# Revit family: SSF type 1,2,3,5 and 6
name_source: partatom
category: Windows
revit_build: Autodesk Revit LT 2016 (Build: 20150220_1215(x64)
units: mm (PartAtom-declared; Revit-internal decimal feet)

## family parameters
Always vertical = Yes
Cut with Voids When Loaded = No
Host = Wall
OmniClass Number = 23.30.20.00
OmniClass Title = Windows
Room Calculation Point = No
Shared = No

## types (30) — shared parameters
Default Sill Height = 914.4 mm  [stored 3 ft]
Frame putty = Glazing putty
GB 2 = 922.2 mm
GB 3 = 1390.2 mm
GB 4 = 1856.2 mm
Glass = Glass
Glazing 3 = Yes
Glazing bar = Steel dipped in Grey oxide
Glazing bar 6 = No
Manufacturer = Robmeg
Vert GB LT = No
Vert GB RT = No
Wall Closure = By host

## per-type parameters (varying)
- SS type- SSF56: Description=Industrial steel window; GB 1=456.2 mm; GB 5=2322.2 mm; GB 6=2790.2 mm; GB LT=780.6 mm; GB RT=780.6 mm; Glazing 1=Yes; Glazing 10=Yes; Glazing 11=Yes; Glazing 12=Yes; Glazing 13=Yes; Glazing 14=Yes; Glazing 15=Yes; Glazing 16=Yes; Glazing 17=Yes; Glazing 18=Yes; Glazing 19=Yes; Glazing 2=Yes; Glazing 20=Yes; Glazing 21=Yes; Glazing 22=Yes; Glazing 23=Yes; Glazing 24=Yes; Glazing 25=Yes; Glazing 26=Yes; Glazing 27=Yes; Glazing 28=Yes; Glazing 29=Yes; Glazing 30=Yes; Glazing 4=Yes; Glazing 5=Yes; Glazing 6=Yes; Glazing 7=Yes; Glazing 8=Yes; Glazing 9=Yes; Glazing bar 1=Yes; Glazing bar 2=Yes; Glazing bar 3=Yes; Glazing bar 4=Yes; Glazing bar 5=Yes; Height=2842 mm  [stored 9.32415 ft]; Model=SSF56; URL=www.robmeg.co.za; Vert GB 1=Yes; Vert GB 2=Yes; Vert GB 3=Yes; Vert GB 4=Yes; Vert bar 1=468.36 mm; Vert bar 2=156.12 mm; Vert bar 3=156.12 mm; Vert bar 4=468.36 mm; Width=1613 mm  [stored 5.29199 ft]
- SS type- SSF55: Description=Industrial steel window; GB 1=456.2 mm; GB 5=2322.2 mm; GB 6=2527.2 mm; GB LT=780.6 mm; GB RT=780.6 mm; Glazing 1=Yes; Glazing 10=Yes; Glazing 11=Yes; Glazing 12=Yes; Glazing 13=Yes; Glazing 14=Yes; Glazing 15=Yes; Glazing 16=Yes; Glazing 17=Yes; Glazing 18=Yes; Glazing 19=Yes; Glazing 2=Yes; Glazing 20=Yes; Glazing 21=Yes; Glazing 22=Yes; Glazing 23=Yes; Glazing 24=Yes; Glazing 25=Yes; Glazing 26=No; Glazing 27=No; Glazing 28=No; Glazing 29=No; Glazing 30=No; Glazing 4=Yes; Glazing 5=Yes; Glazing 6=Yes; Glazing 7=Yes; Glazing 8=Yes; Glazing 9=Yes; Glazing bar 1=Yes; Glazing bar 2=Yes; Glazing bar 3=Yes; Glazing bar 4=Yes; Glazing bar 5=No; Height=2374 mm  [stored 7.78871 ft]; Model=SSF55; URL=www.robmeg.co.za; Vert GB 1=Yes; Vert GB 2=Yes; Vert GB 3=Yes; Vert GB 4=Yes; Vert bar 1=468.36 mm; Vert bar 2=156.12 mm; Vert bar 3=156.12 mm; Vert bar 4=468.36 mm; Width=1613 mm  [stored 5.29199 ft]
- SS type- SSF54: Description=Industrial steel window; GB 1=547.2 mm; GB 5=2322.2 mm; GB 6=2527.2 mm; GB LT=780.6 mm; GB RT=780.6 mm; Glazing 1=Yes; Glazing 10=Yes; Glazing 11=Yes; Glazing 12=Yes; Glazing 13=Yes; Glazing 14=Yes; Glazing 15=Yes; Glazing 16=Yes; Glazing 17=Yes; Glazing 18=Yes; Glazing 19=Yes; Glazing 2=Yes; Glazing 20=Yes; Glazing 21=No; Glazing 22=No; Glazing 23=No; Glazing 24=No; Glazing 25=No; Glazing 26=No; Glazing 27=No; Glazing 28=No; Glazing 29=No; Glazing 30=No; Glazing 4=Yes; Glazing 5=Yes; Glazing 6=Yes; Glazing 7=Yes; Glazing 8=Yes; Glazing 9=Yes; Glazing bar 1=Yes; Glazing bar 2=Yes; Glazing bar 3=Yes; Glazing bar 4=No; Glazing bar 5=No; Height=1908 mm  [stored 6.25984 ft]; Model=SSF54; URL=www.robmeg.co.za; Vert GB 1=Yes; Vert GB 2=Yes; Vert GB 3=Yes; Vert GB 4=Yes; Vert bar 1=468.36 mm; Vert bar 2=156.12 mm; Vert bar 3=156.12 mm; Vert bar 4=468.36 mm; Width=1613 mm  [stored 5.29199 ft]
- SS type- SSF53: Description=Industrial steel window; GB 1=547.2 mm; GB 5=2322.2 mm; GB 6=2527.2 mm; GB LT=780.6 mm; GB RT=780.6 mm; Glazing 1=Yes; Glazing 10=Yes; Glazing 11=Yes; Glazing 12=Yes; Glazing 13=Yes; Glazing 14=Yes; Glazing 15=Yes; Glazing 16=No; Glazing 17=No; Glazing 18=No; Glazing 19=No; Glazing 2=Yes; Glazing 20=No; Glazing 21=No; Glazing 22=No; Glazing 23=No; Glazing 24=No; Glazing 25=No; Glazing 26=No; Glazing 27=No; Glazing 28=No; Glazing 29=No; Glazing 30=No; Glazing 4=Yes; Glazing 5=Yes; Glazing 6=Yes; Glazing 7=Yes; Glazing 8=Yes; Glazing 9=Yes; Glazing bar 1=Yes; Glazing bar 2=Yes; Glazing bar 3=No; Glazing bar 4=No; Glazing bar 5=No; Height=1442 mm  [stored 4.73097 ft]; Model=SSF53; URL=www.robmeg.co.za; Vert GB 1=Yes; Vert GB 2=Yes; Vert GB 3=Yes; Vert GB 4=Yes; Vert bar 1=468.36 mm; Vert bar 2=156.12 mm; Vert bar 3=156.12 mm; Vert bar 4=468.36 mm; Width=1613 mm  [stored 5.29199 ft]
- SS type- SSF52: Description=Industrial steel window; GB 1=547.2 mm; GB 5=2322.2 mm; GB 6=2527.2 mm; GB LT=780.6 mm; GB RT=780.6 mm; Glazing 1=Yes; Glazing 10=Yes; Glazing 11=No; Glazing 12=No; Glazing 13=No; Glazing 14=No; Glazing 15=No; Glazing 16=No; Glazing 17=No; Glazing 18=No; Glazing 19=No; Glazing 2=Yes; Glazing 20=No; Glazing 21=No; Glazing 22=No; Glazing 23=No; Glazing 24=No; Glazing 25=No; Glazing 26=No; Glazing 27=No; Glazing 28=No; Glazing 29=No; Glazing 30=No; Glazing 4=Yes; Glazing 5=Yes; Glazing 6=Yes; Glazing 7=Yes; Glazing 8=Yes; Glazing 9=Yes; Glazing bar 1=Yes; Glazing bar 2=No; Glazing bar 3=No; Glazing bar 4=No; Glazing bar 5=No; Height=974 mm  [stored 3.19554 ft]; Model=SSF52; URL=www.robmeg.co.za; Vert GB 1=Yes; Vert GB 2=Yes; Vert GB 3=Yes; Vert GB 4=Yes; Vert bar 1=468.36 mm; Vert bar 2=156.12 mm; Vert bar 3=156.12 mm; Vert bar 4=468.36 mm; Width=1613 mm  [stored 5.29199 ft]
- SS type- SSF51: Description=Industrial steel window; GB 1=456.2 mm; GB 5=2322.2 mm; GB 6=2527.2 mm; GB LT=780.6 mm; GB RT=780.6 mm; Glazing 1=Yes; Glazing 10=No; Glazing 11=No; Glazing 12=No; Glazing 13=No; Glazing 14=No; Glazing 15=No; Glazing 16=No; Glazing 17=No; Glazing 18=No; Glazing 19=No; Glazing 2=Yes; Glazing 20=No; Glazing 21=No; Glazing 22=No; Glazing 23=No; Glazing 24=No; Glazing 25=No; Glazing 26=No; Glazing 27=No; Glazing 28=No; Glazing 29=No; Glazing 30=No; Glazing 4=Yes; Glazing 5=Yes; Glazing 6=No; Glazing 7=No; Glazing 8=No; Glazing 9=No; Glazing bar 1=No; Glazing bar 2=No; Glazing bar 3=No; Glazing bar 4=No; Glazing bar 5=No; Height=508 mm; Model=SSF51; URL=www.robmeg.co.za; Vert GB 1=Yes; Vert GB 2=Yes; Vert GB 3=Yes; Vert GB 4=Yes; Vert bar 1=468.36 mm; Vert bar 2=156.12 mm; Vert bar 3=156.12 mm; Vert bar 4=468.36 mm; Width=1613 mm  [stored 5.29199 ft]
- SS type- SSF46: Description=Industrial steel window; GB 1=456.2 mm; GB 5=2322.2 mm; GB 6=2790.2 mm; GB LT=780.6 mm; GB RT=623.6 mm; Glazing 1=No; Glazing 10=Yes; Glazing 11=No; Glazing 12=Yes; Glazing 13=Yes; Glazing 14=Yes; Glazing 15=Yes; Glazing 16=No; Glazing 17=Yes; Glazing 18=Yes; Glazing 19=Yes; Glazing 2=Yes; Glazing 20=Yes; Glazing 21=No; Glazing 22=Yes; Glazing 23=Yes; Glazing 24=Yes; Glazing 25=Yes; Glazing 26=No; Glazing 27=Yes; Glazing 28=Yes; Glazing 29=Yes; Glazing 30=Yes; Glazing 4=Yes; Glazing 5=Yes; Glazing 6=No; Glazing 7=Yes; Glazing 8=Yes; Glazing 9=Yes; Glazing bar 1=Yes; Glazing bar 2=Yes; Glazing bar 3=Yes; Glazing bar 4=Yes; Glazing bar 5=Yes; Height=2842 mm  [stored 9.32415 ft]; Model=SSF46; URL=www.robmeg.co.za; Vert GB 1=Yes; Vert GB 2=Yes; Vert GB 3=Yes; Vert GB 4=No; Vert bar 1=311.8 mm  [stored 1.02297 ft]; Vert bar 2=0 mm  [stored 0 ft]; Vert bar 3=311.8 mm  [stored 1.02297 ft]; Vert bar 4=623.6 mm; Width=1299 mm  [stored 4.26181 ft]
- SS type- SSF36: Description=Indsutrial steel window; GB 1=456.2 mm; GB 5=2322.2 mm; GB 6=2789.2 mm; GB LT=580.6 mm; GB RT=699.6 mm; Glazing 1=No; Glazing 10=No; Glazing 11=No; Glazing 12=Yes; Glazing 13=Yes; Glazing 14=Yes; Glazing 15=No; Glazing 16=No; Glazing 17=Yes; Glazing 18=Yes; Glazing 19=Yes; Glazing 2=Yes; Glazing 20=No; Glazing 21=No; Glazing 22=Yes; Glazing 23=Yes; Glazing 24=Yes; Glazing 25=No; Glazing 26=No; Glazing 27=Yes; Glazing 28=Yes; Glazing 29=Yes; Glazing 30=No; Glazing 4=Yes; Glazing 5=No; Glazing 6=No; Glazing 7=Yes; Glazing 8=Yes; Glazing 9=Yes; Glazing bar 1=Yes; Glazing bar 2=Yes; Glazing bar 3=Yes; Glazing bar 4=Yes; Glazing bar 5=Yes; Height=2842 mm  [stored 9.32415 ft]; Model=SSF36; URL=www.robmeg.co.za; Vert GB 1=No; Vert GB 2=Yes; Vert GB 3=Yes; Vert GB 4=No; Vert bar 1=468.36 mm; Vert bar 2=156.12 mm; Vert bar 3=156.12 mm; Vert bar 4=468.36 mm; Width=984 mm  [stored 3.22835 ft]
- SS type- SSF45: Description=Industrial steel window; GB 1=456.2 mm; GB 5=2323.2 mm; GB 6=2790.2 mm; GB LT=780.6 mm; GB RT=623.6 mm; Glazing 1=No; Glazing 10=Yes; Glazing 11=No; Glazing 12=Yes; Glazing 13=Yes; Glazing 14=Yes; Glazing 15=Yes; Glazing 16=No; Glazing 17=Yes; Glazing 18=Yes; Glazing 19=Yes; Glazing 2=Yes; Glazing 20=Yes; Glazing 21=No; Glazing 22=Yes; Glazing 23=Yes; Glazing 24=Yes; Glazing 25=Yes; Glazing 26=No; Glazing 27=No; Glazing 28=No; Glazing 29=No; Glazing 30=No; Glazing 4=Yes; Glazing 5=Yes; Glazing 6=No; Glazing 7=Yes; Glazing 8=Yes; Glazing 9=Yes; Glazing bar 1=Yes; Glazing bar 2=Yes; Glazing bar 3=Yes; Glazing bar 4=Yes; Glazing bar 5=No; Height=2375 mm; Model=SSF45; URL=www.robmeg.co.za; Vert GB 1=Yes; Vert GB 2=Yes; Vert GB 3=Yes; Vert GB 4=No; Vert bar 1=311.8 mm  [stored 1.02297 ft]; Vert bar 2=0 mm  [stored 0 ft]; Vert bar 3=311.8 mm  [stored 1.02297 ft]; Vert bar 4=623.6 mm; Width=1299 mm  [stored 4.26181 ft]
- SS type- SSF44: GB 1=456.2 mm; GB 5=2323.2 mm; GB 6=2790.2 mm; GB LT=780.6 mm; GB RT=623.6 mm; Glazing 1=No; Glazing 10=Yes; Glazing 11=No; Glazing 12=Yes; Glazing 13=Yes; Glazing 14=Yes; Glazing 15=Yes; Glazing 16=No; Glazing 17=Yes; Glazing 18=Yes; Glazing 19=Yes; Glazing 2=Yes; Glazing 20=Yes; Glazing 21=No; Glazing 22=No; Glazing 23=No; Glazing 24=No; Glazing 25=No; Glazing 26=No; Glazing 27=No; Glazing 28=No; Glazing 29=No; Glazing 30=No; Glazing 4=Yes; Glazing 5=Yes; Glazing 6=No; Glazing 7=Yes; Glazing 8=Yes; Glazing 9=Yes; Glazing bar 1=Yes; Glazing bar 2=Yes; Glazing bar 3=Yes; Glazing bar 4=No; Glazing bar 5=No; Height=1908 mm  [stored 6.25984 ft]; Vert GB 1=Yes; Vert GB 2=Yes; Vert GB 3=Yes; Vert GB 4=No; Vert bar 1=311.8 mm  [stored 1.02297 ft]; Vert bar 2=0 mm  [stored 0 ft]; Vert bar 3=311.8 mm  [stored 1.02297 ft]; Vert bar 4=623.6 mm; Width=1299 mm  [stored 4.26181 ft]
- SS type- SSF43: Description=Industrial steel window; GB 1=456.2 mm; GB 5=2323.2 mm; GB 6=2790.2 mm; GB LT=780.6 mm; GB RT=623.6 mm; Glazing 1=No; Glazing 10=Yes; Glazing 11=No; Glazing 12=Yes; Glazing 13=Yes; Glazing 14=Yes; Glazing 15=Yes; Glazing 16=No; Glazing 17=No; Glazing 18=Yes; Glazing 19=No; Glazing 2=Yes; Glazing 20=No; Glazing 21=No; Glazing 22=No; Glazing 23=No; Glazing 24=No; Glazing 25=No; Glazing 26=No; Glazing 27=No; Glazing 28=No; Glazing 29=No; Glazing 30=No; Glazing 4=Yes; Glazing 5=Yes; Glazing 6=No; Glazing 7=Yes; Glazing 8=Yes; Glazing 9=Yes; Glazing bar 1=Yes; Glazing bar 2=Yes; Glazing bar 3=No; Glazing bar 4=No; Glazing bar 5=No; Height=1442 mm  [stored 4.73097 ft]; Model=SSF43; URL=www.robmeg.co.za; Vert GB 1=Yes; Vert GB 2=Yes; Vert GB 3=Yes; Vert GB 4=No; Vert bar 1=311.8 mm  [stored 1.02297 ft]; Vert bar 2=0 mm  [stored 0 ft]; Vert bar 3=311.8 mm  [stored 1.02297 ft]; Vert bar 4=623.6 mm; Width=1299 mm  [stored 4.26181 ft]
- SS type- SSF42: Description=Industrial steel window; GB 1=456.2 mm; GB 5=2323.2 mm; GB 6=2790.2 mm; GB LT=780.6 mm; GB RT=623.6 mm; Glazing 1=No; Glazing 10=Yes; Glazing 11=No; Glazing 12=No; Glazing 13=Yes; Glazing 14=No; Glazing 15=No; Glazing 16=No; Glazing 17=No; Glazing 18=No; Glazing 19=No; Glazing 2=Yes; Glazing 20=No; Glazing 21=No; Glazing 22=No; Glazing 23=No; Glazing 24=No; Glazing 25=No; Glazing 26=No; Glazing 27=No; Glazing 28=No; Glazing 29=No; Glazing 30=No; Glazing 4=Yes; Glazing 5=Yes; Glazing 6=No; Glazing 7=Yes; Glazing 8=Yes; Glazing 9=Yes; Glazing bar 1=Yes; Glazing bar 2=No; Glazing bar 3=No; Glazing bar 4=No; Glazing bar 5=No; Height=975 mm  [stored 3.19882 ft]; Model=SSF42; URL=www.robmeg.co.za; Vert GB 1=Yes; Vert GB 2=Yes; Vert GB 3=Yes; Vert GB 4=No; Vert bar 1=311.8 mm  [stored 1.02297 ft]; Vert bar 2=0 mm  [stored 0 ft]; Vert bar 3=311.8 mm  [stored 1.02297 ft]; Vert bar 4=623.6 mm; Width=1299 mm  [stored 4.26181 ft]
- SS type- SSF41: Description=Industrial steel window; GB 1=456.2 mm; GB 5=2323.2 mm; GB 6=2790.2 mm; GB LT=780.6 mm; GB RT=623.6 mm; Glazing 1=No; Glazing 10=No; Glazing 11=No; Glazing 12=No; Glazing 13=No; Glazing 14=No; Glazing 15=No; Glazing 16=No; Glazing 17=No; Glazing 18=No; Glazing 19=No; Glazing 2=Yes; Glazing 20=No; Glazing 21=No; Glazing 22=No; Glazing 23=No; Glazing 24=No; Glazing 25=No; Glazing 26=No; Glazing 27=No; Glazing 28=No; Glazing 29=No; Glazing 30=No; Glazing 4=Yes; Glazing 5=Yes; Glazing 6=No; Glazing 7=No; Glazing 8=No; Glazing 9=No; Glazing bar 1=No; Glazing bar 2=No; Glazing bar 3=No; Glazing bar 4=No; Glazing bar 5=No; Height=508 mm; Model=SSF41; URL=www.robmeg.co.za; Vert GB 1=Yes; Vert GB 2=Yes; Vert GB 3=Yes; Vert GB 4=No; Vert bar 1=311.8 mm  [stored 1.02297 ft]; Vert bar 2=0 mm  [stored 0 ft]; Vert bar 3=311.8 mm  [stored 1.02297 ft]; Vert bar 4=623.6 mm; Width=1299 mm  [stored 4.26181 ft]
- SS type- SSF35: Description=Industrial steel windows; GB 1=456.2 mm; GB 5=2322.2 mm; GB 6=2789.2 mm; GB LT=580.6 mm; GB RT=699.6 mm; Glazing 1=No; Glazing 10=No; Glazing 11=No; Glazing 12=Yes; Glazing 13=Yes; Glazing 14=Yes; Glazing 15=No; Glazing 16=No; Glazing 17=Yes; Glazing 18=Yes; Glazing 19=Yes; Glazing 2=Yes; Glazing 20=No; Glazing 21=No; Glazing 22=Yes; Glazing 23=Yes; Glazing 24=Yes; Glazing 25=No; Glazing 26=No; Glazing 27=No; Glazing 28=No; Glazing 29=No; Glazing 30=No; Glazing 4=Yes; Glazing 5=No; Glazing 6=No; Glazing 7=Yes; Glazing 8=Yes; Glazing 9=Yes; Glazing bar 1=Yes; Glazing bar 2=Yes; Glazing bar 3=Yes; Glazing bar 4=Yes; Glazing bar 5=No; Height=2375 mm; Model=SSF35; URL=www.robmeg.co.za; Vert GB 1=No; Vert GB 2=Yes; Vert GB 3=Yes; Vert GB 4=No; Vert bar 1=468.36 mm; Vert bar 2=156.12 mm; Vert bar 3=156.12 mm; Vert bar 4=468.36 mm; Width=984 mm  [stored 3.22835 ft]
- SS type- SSF34: Description=Industrial steel windows; GB 1=456.2 mm; GB 5=2322.2 mm; GB 6=2789.2 mm; GB LT=580.6 mm; GB RT=699.6 mm; Glazing 1=No; Glazing 10=No; Glazing 11=No; Glazing 12=Yes; Glazing 13=Yes; Glazing 14=Yes; Glazing 15=No; Glazing 16=No; Glazing 17=Yes; Glazing 18=Yes; Glazing 19=Yes; Glazing 2=Yes; Glazing 20=No; Glazing 21=No; Glazing 22=No; Glazing 23=No; Glazing 24=No; Glazing 25=No; Glazing 26=No; Glazing 27=No; Glazing 28=No; Glazing 29=No; Glazing 30=No; Glazing 4=Yes; Glazing 5=No; Glazing 6=No; Glazing 7=Yes; Glazing 8=Yes; Glazing 9=Yes; Glazing bar 1=Yes; Glazing bar 2=Yes; Glazing bar 3=Yes; Glazing bar 4=No; Glazing bar 5=No; Height=1908 mm  [stored 6.25984 ft]; Model=SSF34; URL=www.robmeg.co.za; Vert GB 1=No; Vert GB 2=Yes; Vert GB 3=Yes; Vert GB 4=No; Vert bar 1=468.36 mm; Vert bar 2=156.12 mm; Vert bar 3=156.12 mm; Vert bar 4=468.36 mm; Width=984 mm  [stored 3.22835 ft]
- SS type- SSF33: Description=Industrial steel windows; GB 1=456.2 mm; GB 5=2322.2 mm; GB 6=2789.2 mm; GB LT=580.6 mm; GB RT=699.6 mm; Glazing 1=No; Glazing 10=No; Glazing 11=No; Glazing 12=Yes; Glazing 13=Yes; Glazing 14=Yes; Glazing 15=No; Glazing 16=No; Glazing 17=No; Glazing 18=No; Glazing 19=No; Glazing 2=Yes; Glazing 20=No; Glazing 21=No; Glazing 22=No; Glazing 23=No; Glazing 24=No; Glazing 25=No; Glazing 26=No; Glazing 27=No; Glazing 28=No; Glazing 29=No; Glazing 30=No; Glazing 4=Yes; Glazing 5=No; Glazing 6=No; Glazing 7=Yes; Glazing 8=Yes; Glazing 9=Yes; Glazing bar 1=Yes; Glazing bar 2=Yes; Glazing bar 3=No; Glazing bar 4=No; Glazing bar 5=No; Height=1442 mm  [stored 4.73097 ft]; Model=SSF33; URL=www.robmeg.co.za; Vert GB 1=No; Vert GB 2=Yes; Vert GB 3=Yes; Vert GB 4=No; Vert bar 1=468.36 mm; Vert bar 2=156.12 mm; Vert bar 3=156.12 mm; Vert bar 4=468.36 mm; Width=984 mm  [stored 3.22835 ft]
- SS type- SSF32: Description=Industrial steel windows; GB 1=456.2 mm; GB 5=2322.2 mm; GB 6=2789.2 mm; GB LT=580.6 mm; GB RT=699.6 mm; Glazing 1=No; Glazing 10=No; Glazing 11=No; Glazing 12=No; Glazing 13=Yes; Glazing 14=No; Glazing 15=No; Glazing 16=No; Glazing 17=No; Glazing 18=No; Glazing 19=No; Glazing 2=Yes; Glazing 20=No; Glazing 21=No; Glazing 22=No; Glazing 23=No; Glazing 24=No; Glazing 25=No; Glazing 26=No; Glazing 27=No; Glazing 28=No; Glazing 29=No; Glazing 30=No; Glazing 4=Yes; Glazing 5=No; Glazing 6=No; Glazing 7=Yes; Glazing 8=Yes; Glazing 9=Yes; Glazing bar 1=Yes; Glazing bar 2=No; Glazing bar 3=No; Glazing bar 4=No; Glazing bar 5=No; Height=975 mm  [stored 3.19882 ft]; Model=SSF32; URL=www.robmeg.co.za; Vert GB 1=No; Vert GB 2=Yes; Vert GB 3=Yes; Vert GB 4=No; Vert bar 1=468.36 mm; Vert bar 2=156.12 mm; Vert bar 3=156.12 mm; Vert bar 4=468.36 mm; Width=984 mm  [stored 3.22835 ft]
- SS type- SSF31: Description=Industrial steel windows; GB 1=456.2 mm; GB 5=2322.2 mm; GB 6=2789.2 mm; GB LT=580.6 mm; GB RT=699.6 mm; Glazing 1=No; Glazing 10=No; Glazing 11=No; Glazing 12=No; Glazing 13=No; Glazing 14=No; Glazing 15=No; Glazing 16=No; Glazing 17=No; Glazing 18=No; Glazing 19=No; Glazing 2=Yes; Glazing 20=No; Glazing 21=No; Glazing 22=No; Glazing 23=No; Glazing 24=No; Glazing 25=No; Glazing 26=No; Glazing 27=No; Glazing 28=No; Glazing 29=No; Glazing 30=No; Glazing 4=Yes; Glazing 5=No; Glazing 6=No; Glazing 7=No; Glazing 8=No; Glazing 9=No; Glazing bar 1=No; Glazing bar 2=No; Glazing bar 3=No; Glazing bar 4=No; Glazing bar 5=No; Height=508 mm; Model=SSF31; URL=www.robmeg.co.za; Vert GB 1=No; Vert GB 2=Yes; Vert GB 3=Yes; Vert GB 4=No; Vert bar 1=468.36 mm; Vert bar 2=156.12 mm; Vert bar 3=156.12 mm; Vert bar 4=468.36 mm; Width=984 mm  [stored 3.22835 ft]
- SS type- SSF26: Description=Industrial steel windows; GB 1=456.2 mm; GB 5=2322.2 mm; GB 6=2789.2 mm; GB LT=580.6 mm; GB RT=699.6 mm; Glazing 1=No; Glazing 10=No; Glazing 11=No; Glazing 12=Yes; Glazing 13=Yes; Glazing 14=No; Glazing 15=No; Glazing 16=No; Glazing 17=Yes; Glazing 18=Yes; Glazing 19=No; Glazing 2=Yes; Glazing 20=No; Glazing 21=No; Glazing 22=Yes; Glazing 23=Yes; Glazing 24=No; Glazing 25=No; Glazing 26=No; Glazing 27=Yes; Glazing 28=Yes; Glazing 29=No; Glazing 30=No; Glazing 4=No; Glazing 5=No; Glazing 6=No; Glazing 7=Yes; Glazing 8=Yes; Glazing 9=No; Glazing bar 1=Yes; Glazing bar 2=Yes; Glazing bar 3=Yes; Glazing bar 4=Yes; Glazing bar 5=Yes; Height=2842 mm  [stored 9.32415 ft]; Model=SSF26; URL=www.robmeg.co.za; Vert GB 1=No; Vert GB 2=No; Vert GB 3=Yes; Vert GB 4=No; Vert bar 1=623.6 mm; Vert bar 2=466.1 mm; Vert bar 3=0 mm  [stored 0 ft]; Vert bar 4=468.36 mm; Width=984 mm  [stored 3.22835 ft]
- SS type- SSF25: Description=Indsutrial steel windows; GB 1=456.2 mm; GB 5=2322.2 mm; GB 6=2789.2 mm; GB LT=580.6 mm; GB RT=699.6 mm; Glazing 1=No; Glazing 10=No; Glazing 11=No; Glazing 12=Yes; Glazing 13=Yes; Glazing 14=No; Glazing 15=No; Glazing 16=No; Glazing 17=Yes; Glazing 18=Yes; Glazing 19=No; Glazing 2=Yes; Glazing 20=No; Glazing 21=No; Glazing 22=Yes; Glazing 23=Yes; Glazing 24=No; Glazing 25=No; Glazing 26=No; Glazing 27=No; Glazing 28=No; Glazing 29=No; Glazing 30=No; Glazing 4=No; Glazing 5=No; Glazing 6=No; Glazing 7=Yes; Glazing 8=Yes; Glazing 9=No; Glazing bar 1=Yes; Glazing bar 2=Yes; Glazing bar 3=Yes; Glazing bar 4=Yes; Glazing bar 5=No; Height=2375 mm; Model=SSF25; URL=www.robmeg.co.za; Vert GB 1=No; Vert GB 2=No; Vert GB 3=Yes; Vert GB 4=No; Vert bar 1=623.6 mm; Vert bar 2=466.1 mm; Vert bar 3=0 mm  [stored 0 ft]; Vert bar 4=468.36 mm; Width=984 mm  [stored 3.22835 ft]
- SS type- SSF24: Description=Industrial steel windows; GB 1=456.2 mm; GB 5=2322.2 mm; GB 6=2789.2 mm; GB LT=580.6 mm; GB RT=699.6 mm; Glazing 1=No; Glazing 10=No; Glazing 11=No; Glazing 12=Yes; Glazing 13=Yes; Glazing 14=No; Glazing 15=No; Glazing 16=No; Glazing 17=Yes; Glazing 18=Yes; Glazing 19=No; Glazing 2=Yes; Glazing 20=No; Glazing 21=No; Glazing 22=No; Glazing 23=No; Glazing 24=No; Glazing 25=No; Glazing 26=No; Glazing 27=No; Glazing 28=No; Glazing 29=No; Glazing 30=No; Glazing 4=No; Glazing 5=No; Glazing 6=No; Glazing 7=Yes; Glazing 8=Yes; Glazing 9=No; Glazing bar 1=Yes; Glazing bar 2=Yes; Glazing bar 3=Yes; Glazing bar 4=No; Glazing bar 5=No; Height=1908 mm  [stored 6.25984 ft]; Model=SSF24; URL=www.robmeg.co.za; Vert GB 1=No; Vert GB 2=No; Vert GB 3=Yes; Vert GB 4=No; Vert bar 1=623.6 mm; Vert bar 2=466.1 mm; Vert bar 3=0 mm  [stored 0 ft]; Vert bar 4=468.36 mm; Width=984 mm  [stored 3.22835 ft]
- SS type- SSF23: Description=Industrial steel windows; GB 1=456.2 mm; GB 5=2322.2 mm; GB 6=2789.2 mm; GB LT=580.6 mm; GB RT=699.6 mm; Glazing 1=No; Glazing 10=No; Glazing 11=No; Glazing 12=Yes; Glazing 13=Yes; Glazing 14=No; Glazing 15=No; Glazing 16=No; Glazing 17=No; Glazing 18=No; Glazing 19=No; Glazing 2=Yes; Glazing 20=No; Glazing 21=No; Glazing 22=No; Glazing 23=No; Glazing 24=No; Glazing 25=No; Glazing 26=No; Glazing 27=No; Glazing 28=No; Glazing 29=No; Glazing 30=No; Glazing 4=No; Glazing 5=No; Glazing 6=No; Glazing 7=Yes; Glazing 8=Yes; Glazing 9=No; Glazing bar 1=Yes; Glazing bar 2=Yes; Glazing bar 3=No; Glazing bar 4=No; Glazing bar 5=No; Height=1442 mm  [stored 4.73097 ft]; Model=SSF23; URL=www.robmeg.co.za; Vert GB 1=No; Vert GB 2=No; Vert GB 3=Yes; Vert GB 4=No; Vert bar 1=623.6 mm; Vert bar 2=466.1 mm; Vert bar 3=0 mm  [stored 0 ft]; Vert bar 4=468.36 mm; Width=984 mm  [stored 3.22835 ft]
- SS type- SSF22: Description=Industrial steel windows; GB 1=456.2 mm; GB 5=2322.2 mm; GB 6=2789.2 mm; GB LT=580.6 mm; GB RT=699.6 mm; Glazing 1=No; Glazing 10=No; Glazing 11=No; Glazing 12=No; Glazing 13=No; Glazing 14=No; Glazing 15=No; Glazing 16=No; Glazing 17=No; Glazing 18=No; Glazing 19=No; Glazing 2=Yes; Glazing 20=No; Glazing 21=No; Glazing 22=No; Glazing 23=No; Glazing 24=No; Glazing 25=No; Glazing 26=No; Glazing 27=No; Glazing 28=No; Glazing 29=No; Glazing 30=No; Glazing 4=No; Glazing 5=No; Glazing 6=No; Glazing 7=Yes; Glazing 8=Yes; Glazing 9=No; Glazing bar 1=Yes; Glazing bar 2=No; Glazing bar 3=No; Glazing bar 4=No; Glazing bar 5=No; Height=975 mm  [stored 3.19882 ft]; Model=SSF22; URL=www.robmeg.co.za; Vert GB 1=No; Vert GB 2=No; Vert GB 3=Yes; Vert GB 4=No; Vert bar 1=623.6 mm; Vert bar 2=466.1 mm; Vert bar 3=0 mm  [stored 0 ft]; Vert bar 4=468.36 mm; Width=984 mm  [stored 3.22835 ft]
- SS type- SSF21: Description=Industrial steel windows; GB 1=456.2 mm; GB 5=2322.2 mm; GB 6=2789.2 mm; GB LT=580.6 mm; GB RT=699.6 mm; Glazing 1=No; Glazing 10=No; Glazing 11=No; Glazing 12=No; Glazing 13=No; Glazing 14=No; Glazing 15=No; Glazing 16=No; Glazing 17=No; Glazing 18=No; Glazing 19=No; Glazing 2=Yes; Glazing 20=No; Glazing 21=No; Glazing 22=No; Glazing 23=No; Glazing 24=No; Glazing 25=No; Glazing 26=No; Glazing 27=No; Glazing 28=No; Glazing 29=No; Glazing 30=No; Glazing 4=No; Glazing 5=No; Glazing 6=No; Glazing 7=No; Glazing 8=No; Glazing 9=No; Glazing bar 1=No; Glazing bar 2=No; Glazing bar 3=No; Glazing bar 4=No; Glazing bar 5=No; Height=508 mm; Model=SSF21; URL=www.robmeg.co.za; Vert GB 1=No; Vert GB 2=No; Vert GB 3=Yes; Vert GB 4=No; Vert bar 1=623.6 mm; Vert bar 2=466.1 mm; Vert bar 3=0 mm  [stored 0 ft]; Vert bar 4=468.36 mm; Width=984 mm  [stored 3.22835 ft]
- SS type- SSF16: Description=Industrial steel windows; GB 1=456.2 mm; GB 5=2322.2 mm; GB 6=2789.2 mm; GB LT=580.6 mm; GB RT=699.6 mm; Glazing 1=No; Glazing 10=No; Glazing 11=No; Glazing 12=No; Glazing 13=Yes; Glazing 14=No; Glazing 15=No; Glazing 16=No; Glazing 17=No; Glazing 18=Yes; Glazing 19=No; Glazing 2=No; Glazing 20=No; Glazing 21=No; Glazing 22=No; Glazing 23=Yes; Glazing 24=No; Glazing 25=No; Glazing 26=No; Glazing 27=No; Glazing 28=Yes; Glazing 29=No; Glazing 30=No; Glazing 4=No; Glazing 5=No; Glazing 6=No; Glazing 7=No; Glazing 8=Yes; Glazing 9=No; Glazing bar 1=Yes; Glazing bar 2=Yes; Glazing bar 3=Yes; Glazing bar 4=Yes; Glazing bar 5=Yes; Height=2842 mm  [stored 9.32415 ft]; Model=SSF16; URL=www.robmeg.co.za; Vert GB 1=No; Vert GB 2=No; Vert GB 3=No; Vert GB 4=No; Vert bar 1=623.6 mm; Vert bar 2=152.1 mm; Vert bar 3=152.1 mm; Vert bar 4=468.36 mm; Width=356 mm  [stored 1.16798 ft]
- SS type- SSF15: Description=Industrial steel windows; GB 1=456.2 mm; GB 5=2322.2 mm; GB 6=2789.2 mm; GB LT=580.6 mm; GB RT=699.6 mm; Glazing 1=No; Glazing 10=No; Glazing 11=No; Glazing 12=No; Glazing 13=Yes; Glazing 14=No; Glazing 15=No; Glazing 16=No; Glazing 17=No; Glazing 18=Yes; Glazing 19=No; Glazing 2=No; Glazing 20=No; Glazing 21=No; Glazing 22=No; Glazing 23=Yes; Glazing 24=No; Glazing 25=No; Glazing 26=No; Glazing 27=No; Glazing 28=No; Glazing 29=No; Glazing 30=No; Glazing 4=No; Glazing 5=No; Glazing 6=No; Glazing 7=No; Glazing 8=Yes; Glazing 9=No; Glazing bar 1=Yes; Glazing bar 2=Yes; Glazing bar 3=Yes; Glazing bar 4=Yes; Glazing bar 5=No; Height=2375 mm; Model=SSF15; URL=www.robmeg.co.za; Vert GB 1=No; Vert GB 2=No; Vert GB 3=No; Vert GB 4=No; Vert bar 1=623.6 mm; Vert bar 2=152.1 mm; Vert bar 3=152.1 mm; Vert bar 4=468.36 mm; Width=356 mm  [stored 1.16798 ft]
- SS type- SSF14: Description=Industrial steel windows; GB 1=456.2 mm; GB 5=2322.2 mm; GB 6=2789.2 mm; GB LT=580.6 mm; GB RT=699.6 mm; Glazing 1=No; Glazing 10=No; Glazing 11=No; Glazing 12=No; Glazing 13=Yes; Glazing 14=No; Glazing 15=No; Glazing 16=No; Glazing 17=No; Glazing 18=Yes; Glazing 19=No; Glazing 2=No; Glazing 20=No; Glazing 21=No; Glazing 22=No; Glazing 23=No; Glazing 24=No; Glazing 25=No; Glazing 26=No; Glazing 27=No; Glazing 28=No; Glazing 29=No; Glazing 30=No; Glazing 4=No; Glazing 5=No; Glazing 6=No; Glazing 7=No; Glazing 8=Yes; Glazing 9=No; Glazing bar 1=Yes; Glazing bar 2=Yes; Glazing bar 3=Yes; Glazing bar 4=No; Glazing bar 5=No; Height=1908 mm  [stored 6.25984 ft]; Model=SSF14; URL=www.robmeg.co.za; Vert GB 1=No; Vert GB 2=No; Vert GB 3=No; Vert GB 4=No; Vert bar 1=623.6 mm; Vert bar 2=152.1 mm; Vert bar 3=152.1 mm; Vert bar 4=468.36 mm; Width=356 mm  [stored 1.16798 ft]
- SS type- SSF13: Description=Industrial steel windows; GB 1=456.2 mm; GB 5=2322.2 mm; GB 6=2789.2 mm; GB LT=580.6 mm; GB RT=699.6 mm; Glazing 1=No; Glazing 10=No; Glazing 11=No; Glazing 12=No; Glazing 13=Yes; Glazing 14=No; Glazing 15=No; Glazing 16=No; Glazing 17=No; Glazing 18=No; Glazing 19=No; Glazing 2=No; Glazing 20=No; Glazing 21=No; Glazing 22=No; Glazing 23=No; Glazing 24=No; Glazing 25=No; Glazing 26=No; Glazing 27=No; Glazing 28=No; Glazing 29=No; Glazing 30=No; Glazing 4=No; Glazing 5=No; Glazing 6=No; Glazing 7=No; Glazing 8=Yes; Glazing 9=No; Glazing bar 1=Yes; Glazing bar 2=Yes; Glazing bar 3=No; Glazing bar 4=No; Glazing bar 5=No; Height=1908 mm  [stored 6.25984 ft]; Model=SSF13; URL=www.robmeg.co.za; Vert GB 1=No; Vert GB 2=No; Vert GB 3=No; Vert GB 4=No; Vert bar 1=623.6 mm; Vert bar 2=152.1 mm; Vert bar 3=152.1 mm; Vert bar 4=468.36 mm; Width=356 mm  [stored 1.16798 ft]
- SS type- SSF12: Description=Industrial steel windows; GB 1=456.2 mm; GB 5=2322.2 mm; GB 6=2789.2 mm; GB LT=580.6 mm; GB RT=699.6 mm; Glazing 1=No; Glazing 10=No; Glazing 11=No; Glazing 12=No; Glazing 13=No; Glazing 14=No; Glazing 15=No; Glazing 16=No; Glazing 17=No; Glazing 18=No; Glazing 19=No; Glazing 2=No; Glazing 20=No; Glazing 21=No; Glazing 22=No; Glazing 23=No; Glazing 24=No; Glazing 25=No; Glazing 26=No; Glazing 27=No; Glazing 28=No; Glazing 29=No; Glazing 30=No; Glazing 4=No; Glazing 5=No; Glazing 6=No; Glazing 7=No; Glazing 8=Yes; Glazing 9=No; Glazing bar 1=Yes; Glazing bar 2=No; Glazing bar 3=No; Glazing bar 4=No; Glazing bar 5=No; Height=975 mm  [stored 3.19882 ft]; Model=SSF12; URL=www.robmeg.co.za; Vert GB 1=No; Vert GB 2=No; Vert GB 3=No; Vert GB 4=No; Vert bar 1=623.6 mm; Vert bar 2=152.1 mm; Vert bar 3=152.1 mm; Vert bar 4=468.36 mm; Width=356 mm  [stored 1.16798 ft]
- SS type- SSF11: Description=Industrial steel windows; GB 1=456.2 mm; GB 5=2322.2 mm; GB 6=2789.2 mm; GB LT=580.6 mm; GB RT=699.6 mm; Glazing 1=No; Glazing 10=No; Glazing 11=No; Glazing 12=No; Glazing 13=No; Glazing 14=No; Glazing 15=No; Glazing 16=No; Glazing 17=No; Glazing 18=No; Glazing 19=No; Glazing 2=No; Glazing 20=No; Glazing 21=No; Glazing 22=No; Glazing 23=No; Glazing 24=No; Glazing 25=No; Glazing 26=No; Glazing 27=No; Glazing 28=No; Glazing 29=No; Glazing 30=No; Glazing 4=No; Glazing 5=No; Glazing 6=No; Glazing 7=No; Glazing 8=No; Glazing 9=No; Glazing bar 1=No; Glazing bar 2=No; Glazing bar 3=No; Glazing bar 4=No; Glazing bar 5=No; Height=508 mm; Model=SSF11; URL=www.robmeg.co.za; Vert GB 1=No; Vert GB 2=No; Vert GB 3=No; Vert GB 4=No; Vert bar 1=623.6 mm; Vert bar 2=152.1 mm; Vert bar 3=152.1 mm; Vert bar 4=468.36 mm; Width=356 mm  [stored 1.16798 ft]

note: [stored X ft] marks values corroborated as IEEE doubles in the binary element streams (Revit-internal decimal feet)

## geometry (parser evidence)
native form markers: Sweep x5
no freeform markers — native parametric forms only
